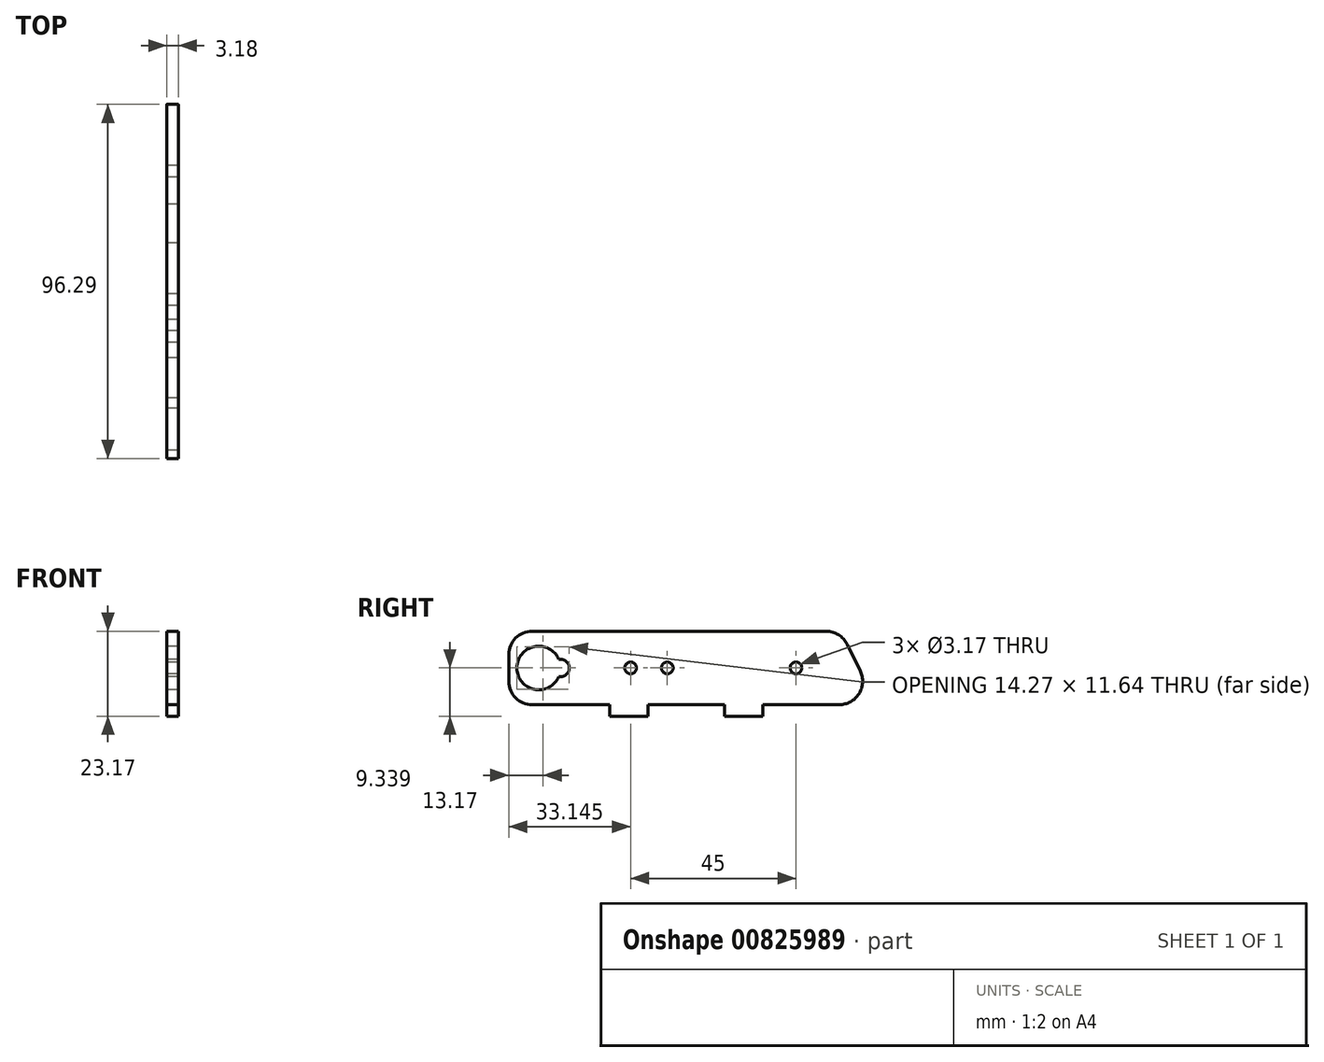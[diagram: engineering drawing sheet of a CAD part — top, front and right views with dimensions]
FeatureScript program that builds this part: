
annotation { "Feature Type Name" : "Feature", "Feature Type Description" : "" }
export const myFeature = defineFeature(function(context is Context, id is Id, definition is map)
    precondition{}
    {
        {
            var Q0;
            Q0=qCreatedBy(makeId("Right.planeOp"),FACE);
            var sketch = newSketch(context, id + "F0", { "sketchPlane" : qUnion([Q0])});
            skLineSegment(sketch, "E0", {"start": v(-32.28, 0) * mm, "end": v(-32.03, 0) * mm});
            skArc(sketch, "E1.filletArc", {"start": v(-38.63, 6.35) * mm, "mid": v(-36.77, 1.86) * mm, "end": v(-32.28, 0) * mm});
            skArc(sketch, "E2.filletArc", {"start": v(51.3, 0) * mm, "mid": v(56.7, 2.98) * mm, "end": v(57.02, 9.13) * mm});
            skArc(sketch, "E3.filletArc", {"start": v(53.46, 16.43) * mm, "mid": v(51.12, 19.03) * mm, "end": v(47.75, 20) * mm});
            skLineSegment(sketch, "E4", {"start": v(53.46, 16.43) * mm, "end": v(57.02, 9.13) * mm});
            skLineSegment(sketch, "E5", {"start": v(-28.72, 20) * mm, "end": v(47.75, 20) * mm});
            skLineSegment(sketch, "E6.top", {"start": v(-11.2, -3.17) * mm, "end": v(-0.78, -3.17) * mm});
            skLineSegment(sketch, "E6.left", {"start": v(-11.2, 0) * mm, "end": v(-11.2, -3.17) * mm});
            skLineSegment(sketch, "E6.right", {"start": v(30.47, 0) * mm, "end": v(30.47, -3.17) * mm});
            skLineSegment(sketch, "E7", {"start": v(20.05, 0) * mm, "end": v(20.05, -3.17) * mm});
            skLineSegment(sketch, "E8", {"start": v(-0.78, 0) * mm, "end": v(-0.78, -3.17) * mm});
            skLineSegment(sketch, "E9.trimOffspring", {"start": v(20.05, -3.17) * mm, "end": v(30.47, -3.17) * mm});
            skLineSegment(sketch, "E10", {"start": v(-32.03, 0) * mm, "end": v(-11.2, 0) * mm});
            skLineSegment(sketch, "E11.trimOffspring", {"start": v(30.47, 0) * mm, "end": v(51.3, 0) * mm});
            skLineSegment(sketch, "E12.trimOffspring", {"start": v(-0.78, 0) * mm, "end": v(20.05, 0) * mm});
            skPoint(sketch, "E13.end.orphan", {"position": v(39.52, 10) * mm});
            skCircle(sketch, "E14", {"center": v(4.52, 10) * mm, "radius": 1.59 * mm});
            skCircle(sketch, "E15", {"center": v(39.52, 10) * mm, "radius": 1.59 * mm});
            skArc(sketch, "E16", {"start": v(-25.02, 12.34) * mm, "mid": v(-36.43, 10) * mm, "end": v(-25.02, 7.66) * mm});
            skArc(sketch, "E17", {"start": v(-25.02, 7.66) * mm, "mid": v(-22.15, 10) * mm, "end": v(-25.02, 12.34) * mm});
            skLineSegment(sketch, "E18.top", {"start": v(-32.28, 20) * mm, "end": v(-28.72, 20) * mm});
            skLineSegment(sketch, "E18.left", {"start": v(-38.63, 6.35) * mm, "end": v(-38.63, 13.65) * mm});
            skArc(sketch, "E19.filletArc", {"start": v(-32.28, 20) * mm, "mid": v(-36.77, 18.14) * mm, "end": v(-38.63, 13.65) * mm});
            skCircle(sketch, "E20", {"center": v(-5.48, 10) * mm, "radius": 1.59 * mm});
            skSolve(sketch);
        }
        {
            var Q0;
            Q0=qSketchRegion(id+"F0",true);
            extrude(context, id + "F1", {"entities" : qUnion([Q0]), "depth" : 3.17 * mm, "offsetDistance" : 25.4 * mm});
        }
    });
